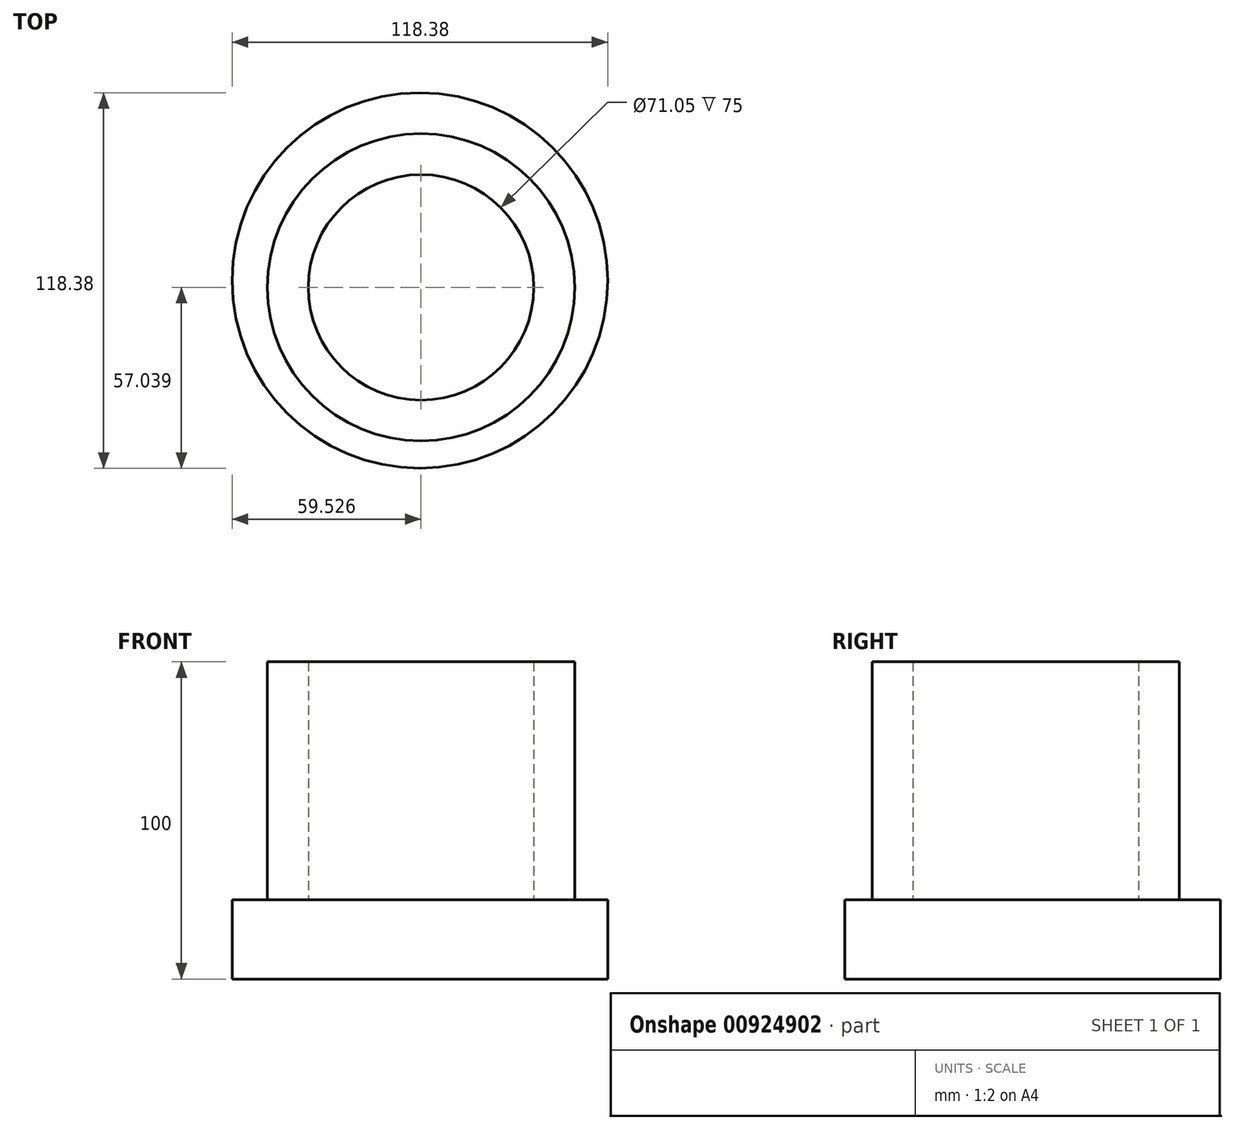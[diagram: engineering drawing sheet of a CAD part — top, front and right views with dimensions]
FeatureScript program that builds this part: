
annotation { "Feature Type Name" : "Feature", "Feature Type Description" : "" }
export const myFeature = defineFeature(function(context is Context, id is Id, definition is map)
    precondition{}
    {
        {
            var Q0;
            Q0=qCreatedBy(makeId("Top.planeOp"),FACE);
            var sketch = newSketch(context, id + "F0", { "sketchPlane" : qUnion([Q0])});
            skCircle(sketch, "E0", {"center": v(-408.8, 0) * mm, "radius": 61.6 * mm});
            skCircle(sketch, "E1", {"center": v(-408.8, 0) * mm, "radius": 83.58 * mm});
            skCircle(sketch, "E2", {"center": v(-408.8, 0) * mm, "radius": 104.28 * mm});
            skSolve(sketch);
        }
        {
            var Q0;
            Q0=makeQuery(id+"F0.imprint","IMPRINT",FACE,{"disambiguationData":[TD([[makeQuery(id+"F0.imprint","IMPRINT",EDGE,{"derivedFrom":sQuery(id+"F0.wireOp",EDGE,"E0")}),-1.0]])]});
            extrude(context, id + "F1", {"entities" : qUnion([Q0]), "depth" : 381 * mm, "offsetDistance" : 25.4 * mm});
        }
        {
            var Q0;
            Q0=makeQuery(id+"F1.opExtrude","CAP_FACE",FACE,{"disambiguationData":[OSD([sQuery(id+"F0.wireOp",EDGE,"E0"),sQuery(id+"F0.wireOp",EDGE,"E1")])],"isStart":false});
            extrude(context, id + "F2", {"entities" : qUnion([Q0]), "operationType" : NewBodyOperationType.ADD, "depth" : 127 * mm, "offsetDistance" : 25.4 * mm});
        }
        {
            var Q0;
            Q0=makeQuery(id+"F1.opExtrude","SWEPT_BODY",BODY,{"disambiguationData":[OSD([sQuery(id+"F0.wireOp",EDGE,"E0"),sQuery(id+"F0.wireOp",EDGE,"E1")])]});
            deleteBodies(context, id + "F3", {"entities" : qUnion([Q0])});
        }
        {
            var Q0;
            Q0=qCreatedBy(makeId("Top.planeOp"),FACE);
            var sketch = newSketch(context, id + "F4", { "sketchPlane" : qUnion([Q0])});
            skCircle(sketch, "E3", {"center": v(-174.2, 12.3) * mm, "radius": 35.53 * mm});
            skCircle(sketch, "E4", {"center": v(-174.2, 12.3) * mm, "radius": 48.42 * mm});
            skSolve(sketch);
        }
        {
            var Q0;
            Q0=makeQuery(id+"F4.imprint","IMPRINT",FACE,{"disambiguationData":[TD([[makeQuery(id+"F4.imprint","IMPRINT",EDGE,{"derivedFrom":sQuery(id+"F4.wireOp",EDGE,"E3")}),-1.0]])]});
            extrude(context, id + "F5", {"entities" : qUnion([Q0]), "depth" : 100 * mm, "offsetDistance" : 25 * mm});
        }
        {
            var Q0;
            Q0=qCreatedBy(makeId("Top.planeOp"),FACE);
            var sketch = newSketch(context, id + "F6", { "sketchPlane" : qUnion([Q0])});
            skCircle(sketch, "E5", {"center": v(-174.53, 14.45) * mm, "radius": 59.2 * mm});
            skSolve(sketch);
        }
        {
            var Q0;
            Q0=makeQuery(id+"F6.imprint","IMPRINT",FACE,{"disambiguationData":[TD([[makeQuery(id+"F6.imprint","IMPRINT",EDGE,{"derivedFrom":sQuery(id+"F6.wireOp",EDGE,"E5")}),1.0]])]});
            extrude(context, id + "F7", {"entities" : qUnion([Q0]), "operationType" : NewBodyOperationType.ADD, "depth" : 25 * mm, "offsetDistance" : 25 * mm});
        }
    });
